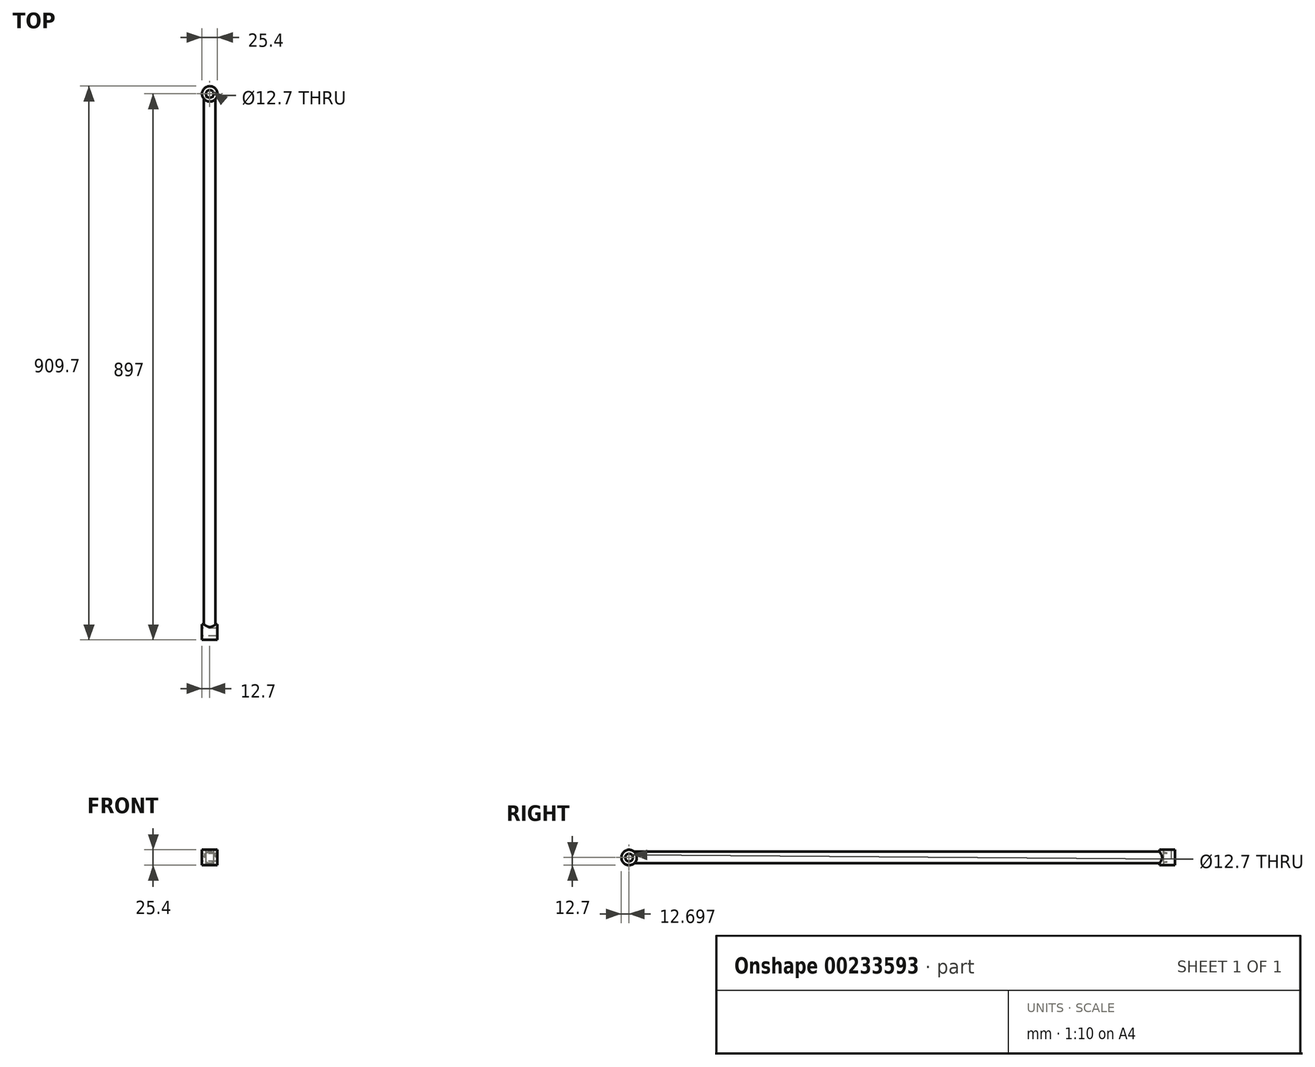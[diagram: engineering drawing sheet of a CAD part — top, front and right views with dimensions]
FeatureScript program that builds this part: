
annotation { "Feature Type Name" : "Feature", "Feature Type Description" : "" }
export const myFeature = defineFeature(function(context is Context, id is Id, definition is map)
    precondition{}
    {
        {
            var Q0;
            Q0=qCreatedBy(makeId("Top.planeOp"),FACE);
            var sketch = newSketch(context, id + "F0", { "sketchPlane" : qUnion([Q0])});
            skCircle(sketch, "E0", {"center": v(0, 0) * mm, "radius": 12.7 * mm});
            skCircle(sketch, "E1", {"center": v(0, 0) * mm, "radius": 6.35 * mm});
            skSolve(sketch);
        }
        {
            var Q0;
            Q0=qCreatedBy(makeId("Front.planeOp"),FACE);
            var sketch = newSketch(context, id + "F1", { "sketchPlane" : qUnion([Q0])});
            skCircle(sketch, "E2", {"center": v(0, 0) * mm, "radius": 9.53 * mm});
            skSolve(sketch);
        }
        {
            var Q0;
            Q0=qSketchRegion(id+"F1",true);
            extrude(context, id + "F2", {"entities" : qUnion([Q0]), "depth" : 876.3 * mm});
        }
        {
            var Q0;
            Q0=makeQuery(id+"F0.imprint","IMPRINT",FACE,{"disambiguationData":[TD([[makeQuery(id+"F0.imprint","IMPRINT",EDGE,{"derivedFrom":sQuery(id+"F0.wireOp",EDGE,"E0")}),1.0]])]});
            extrude(context, id + "F3", {"entities" : qUnion([Q0]), "operationType" : NewBodyOperationType.ADD, "endBound" : BoundingType.SYMMETRIC, "depth" : 25.4 * mm});
        }
        {
            var Q0;
            Q0=makeQuery(id+"F2.opExtrude","CAP_FACE",FACE,{"disambiguationData":[OSD([sQuery(id+"F1.wireOp",EDGE,"E2")])],"isStart":true});
            var Q1;
            Q1=makeQuery(id+"F3.opExtrude","SWEPT_FACE",FACE,{"disambiguationData":[OSD([sQuery(id+"F0.wireOp",EDGE,"E0")])]});
            extrude(context, id + "F4", {"entities" : qUnion([Q0]), "operationType" : NewBodyOperationType.REMOVE, "oppositeDirection" : true, "endBoundEntityFace" : qUnion([Q1]), "depth" : 6.35 * mm});
        }
        {
            var Q0;
            Q0=qCreatedBy(makeId("Right.planeOp"),FACE);
            var sketch = newSketch(context, id + "F5", { "sketchPlane" : qUnion([Q0])});
            skCircle(sketch, "E3", {"center": v(-884.3, 0) * mm, "radius": 12.7 * mm});
            skCircle(sketch, "E4", {"center": v(-884.3, 0) * mm, "radius": 6.35 * mm});
            skSolve(sketch);
        }
        {
            var Q0;
            Q0=makeQuery(id+"F5.imprint","IMPRINT",FACE,{"disambiguationData":[TD([[makeQuery(id+"F5.imprint","IMPRINT",EDGE,{"derivedFrom":sQuery(id+"F5.wireOp",EDGE,"E3")}),1.0]])]});
            extrude(context, id + "F6", {"entities" : qUnion([Q0]), "operationType" : NewBodyOperationType.ADD, "endBound" : BoundingType.SYMMETRIC, "depth" : 25.4 * mm});
        }
    });
